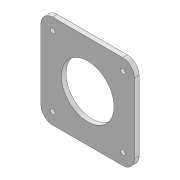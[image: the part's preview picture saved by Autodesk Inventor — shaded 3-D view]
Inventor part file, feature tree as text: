
AUTODESK INVENTOR PART (.ipt)
format: ipt  version: 2020 (Build 240168000, 168)  size: 116,736 bytes
history: native  units: mm
features: other x5, extrude x1
ambient origin geometry x8: Origin, YZ Plane, XZ Plane, XY Plane, X Axis, Y Axis, Z Axis, Center Point
bodies: Body1 (feature_tree)
feature tree (6):
  other  "Sólido1"
  other  "Plano de trabalho1"
  extrude  "Extrusão1"  Depth=45.0mm
  other  "<userpath>\OneDrive\Área de Trabalho\Calorimetro 2022\Inventor\parte_superior.iam"
  other  "parte_superior.iam"
  other  "Corpo_1:4"
